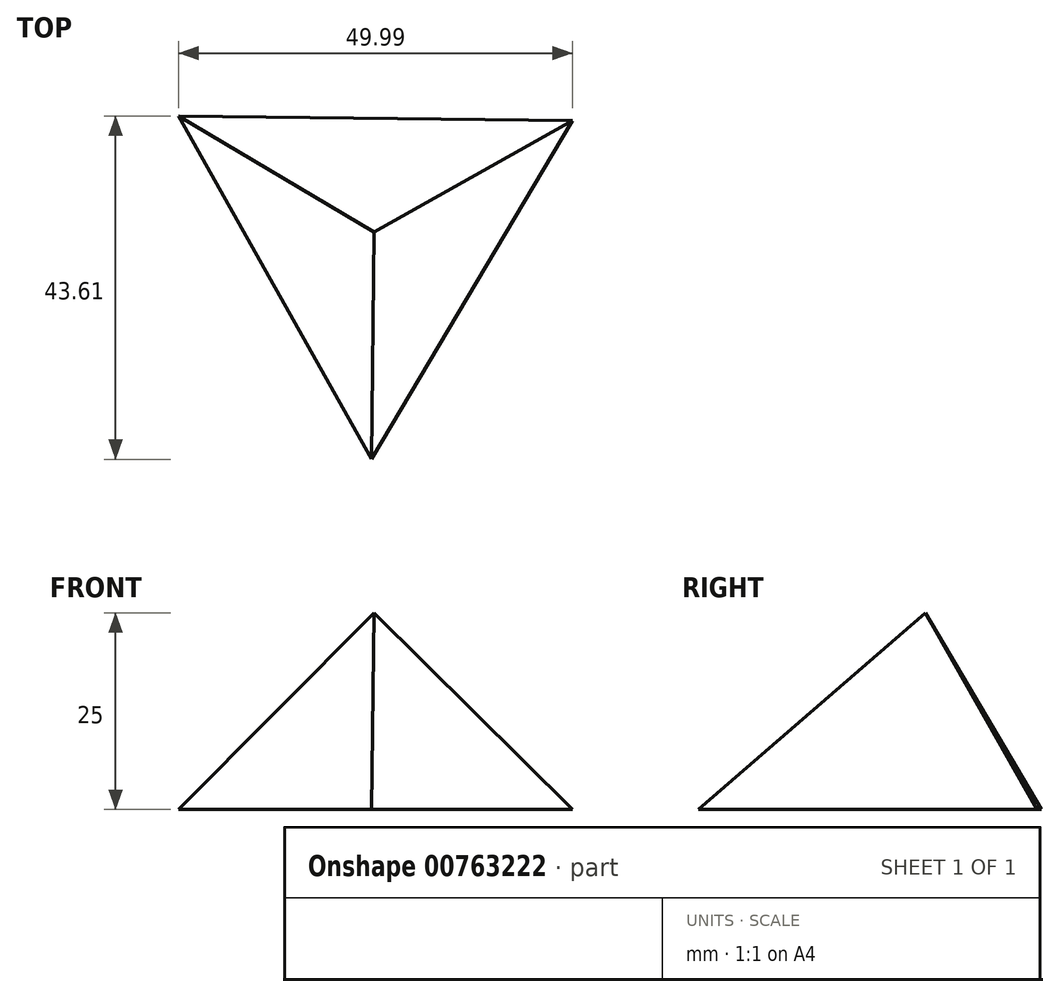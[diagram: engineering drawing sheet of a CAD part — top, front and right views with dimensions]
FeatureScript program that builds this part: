
annotation { "Feature Type Name" : "Feature", "Feature Type Description" : "" }
export const myFeature = defineFeature(function(context is Context, id is Id, definition is map)
    precondition{}
    {
        {
            var Q0;
            Q0=qCreatedBy(makeId("Top.planeOp"),FACE);
            var sketch = newSketch(context, id + "F0", { "sketchPlane" : qUnion([Q0])});
            skCircle(sketch, "E0.cCircle", {"center": v(0, 0) * mm, "radius": 28.87 * mm, "construction": true});
            skLineSegment(sketch, "E0.0", {"start": v(-24.82, 14.74) * mm, "end": v(25.17, 14.13) * mm});
            skLineSegment(sketch, "E0.1", {"start": v(25.17, 14.13) * mm, "end": v(-0.35, -28.87) * mm});
            skLineSegment(sketch, "E0.2", {"start": v(-0.35, -28.87) * mm, "end": v(-24.82, 14.74) * mm});
            skSolve(sketch);
        }
        {
            var Q0;
            Q0 = qSketchRegion(id + "F0", true);
            extrude(context, id + "F1", {"entities" : qUnion([Q0]), "depth" : 50 * mm, "offsetDistance" : 25 * mm, "hasDraft" : true, "draftAngle" : 30 * degree, "draftPullDirection" : true});
        }
    });
